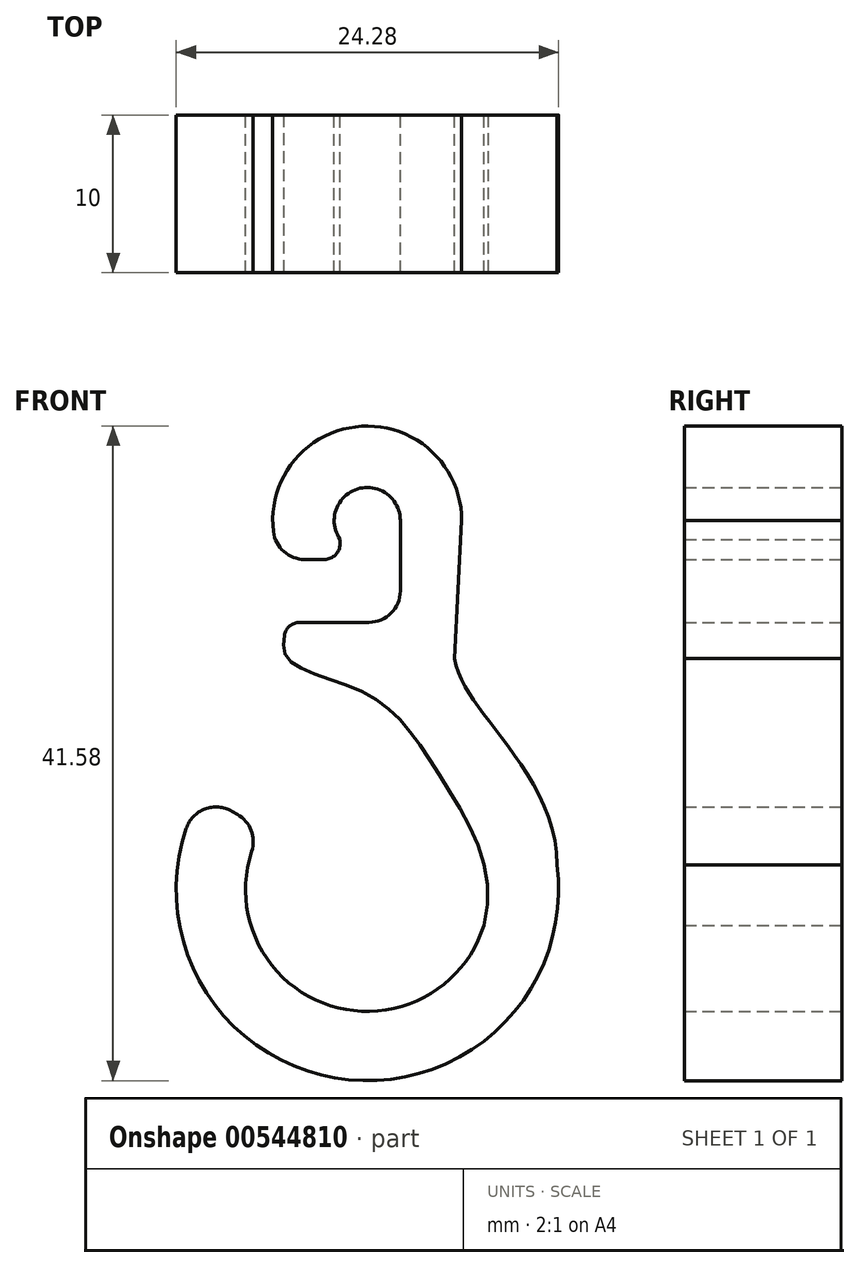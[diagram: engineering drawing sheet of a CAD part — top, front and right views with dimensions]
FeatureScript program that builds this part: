
annotation { "Feature Type Name" : "Feature", "Feature Type Description" : "" }
export const myFeature = defineFeature(function(context is Context, id is Id, definition is map)
    precondition{}
    {
        {
            var Q0;
            Q0=qCreatedBy(makeId("Front.planeOp"),FACE);
            var sketch = newSketch(context, id + "F0", { "sketchPlane" : qUnion([Q0])});
            skCircle(sketch, "E0", {"center": v(0, 0) * mm, "radius": 2.1 * mm});
            skLineSegment(sketch, "E1", {"start": v(2.1, 0) * mm, "end": v(2.1, -8.07) * mm});
            skArc(sketch, "E2", {"start": v(5.47, -2.47) * mm, "mid": v(0, 6) * mm, "end": v(-5.47, -2.47) * mm});
            skLineSegment(sketch, "E3", {"start": v(-5.13, -6.47) * mm, "end": v(-1.73, -6.47) * mm});
            skLineSegment(sketch, "E4", {"start": v(-5.47, -2.47) * mm, "end": v(-1.73, -2.47) * mm});
            skLineSegment(sketch, "E5", {"start": v(-1.73, -2.47) * mm, "end": v(-1.73, -1.2) * mm});
            skLineSegment(sketch, "E6", {"start": v(-1.73, -6.47) * mm, "end": v(-1.73, -6.98) * mm});
            skArc(sketch, "E7", {"start": v(-10.5, -17.36) * mm, "mid": v(-2.37, -35.34) * mm, "end": v(12.05, -21.86) * mm});
            skArc(sketch, "E8.0", {"start": v(-6.7, -19.56) * mm, "mid": v(-3.09, -30.53) * mm, "end": v(7.4, -25.72) * mm});
            skLineSegment(sketch, "E9", {"start": v(-10.5, -17.36) * mm, "end": v(-6.7, -19.56) * mm});
            skLineSegment(sketch, "E10", {"start": v(-1.73, -6.47) * mm, "end": v(2.1, -6.47) * mm});
            skLineSegment(sketch, "E11", {"start": v(6, 0) * mm, "end": v(5.54, -8.76) * mm});
            skFitSpline(sketch, "E12", {"points": [v(5.54, -8.76) * mm, v(7.96, -13.04) * mm, v(12.05, -21.86) * mm], "startDerivative": vector(2.22, -10.9) * mm, "endDerivative": vector(-0.13, -18.18) * mm});
            skFitSpline(sketch, "E13", {"points": [v(-5.13, -6.47) * mm, v(-5.13, -8.67) * mm, v(0, -11.04) * mm, v(4.6, -16.17) * mm, v(7.4, -25.72) * mm], "startDerivative": vector(-1.47, -13.57) * mm, "endDerivative": vector(-9.36, -32.54) * mm});
            skSolve(sketch);
        }
        {
            var Q0;
            Q0=makeQuery(id+"F0.imprint","IMPRINT",FACE,{"disambiguationData":[TD([[makeQuery(id+"F0.imprint","IMPRINT",EDGE,{"derivedFrom":sQuery(id+"F0.wireOp",EDGE,"E7")}),1.0]])]});
            var Q1;
            {var subQ7=sQuery(id+"F0.wireOp",EDGE,"E1");Q1=makeQuery(id+"F0.imprint","IMPRINT",FACE,{"disambiguationData":[TD([[makeQuery(id+"F0.imprint","IMPRINT",EDGE,{"derivedFrom":subQ7}),1.0]])]});}
            var Q2;
            {var subQ0=sQuery(id+"F0.wireOp",EDGE,"oHz4fgxV-5wzr-duW4-scc5-XEAWSv9MsjhE");var subQ1=makeQuery(id+"F0.imprint","INTERSECT",VERTEX,{"derivedFrom":[subQ0,sQuery(id+"F0.wireOp",EDGE,"E1")]});Q2=makeQuery(id+"F0.imprint","IMPRINT",FACE,{"disambiguationData":[TD([[makeQuery(id+"F0.imprint","IMPRINT",EDGE,{"disambiguationData":[TD([[subQ1,-1.0]])],"derivedFrom":subQ0}),1.0]])]});}
            var Q3;
            {var subQ3=sQuery(id+"F0.wireOp",EDGE,"E6");Q3=makeQuery(id+"F0.imprint","IMPRINT",FACE,{"disambiguationData":[TD([[makeQuery(id+"F0.imprint","IMPRINT",EDGE,{"derivedFrom":subQ3}),1.0]])]});}
            extrude(context, id + "F1", {"entities" : qUnion([Q0, Q1, Q2, Q3]), "depth" : 10 * mm, "offsetDistance" : 25 * mm});
        }
        {
            var Q0;
            Q0=makeQuery(id+"F1.opExtrude","SWEPT_EDGE",EDGE,{"disambiguationData":[OSD([sQuery(id+"F0.wireOp",EDGE,"E4"),sQuery(id+"F0.wireOp",EDGE,"E5")])]});
            var Q1;
            Q1=makeQuery(id+"F1.opExtrude","SWEPT_EDGE",EDGE,{"disambiguationData":[OSD([sQuery(id+"F0.wireOp",EDGE,"E3"),sQuery(id+"F0.wireOp",EDGE,"E6")])]});
            fillet(context, id + "F2", {"entities" : qUnion([Q0, Q1]), "radius" : 1 * mm, "tangentPropagation" : true, "allowEdgeOverflow" : false});
        }
        {
            var Q0;
            Q0=makeQuery(id+"F1.opExtrude","SWEPT_EDGE",EDGE,{"disambiguationData":[OSD([sQuery(id+"F0.wireOp",EDGE,"E7"),sQuery(id+"F0.wireOp",EDGE,"E9")])]});
            var Q1;
            Q1=makeQuery(id+"F1.opExtrude","SWEPT_EDGE",EDGE,{"disambiguationData":[OSD([sQuery(id+"F0.wireOp",EDGE,"E8.0"),sQuery(id+"F0.wireOp",EDGE,"E9")])]});
            var Q2;
            Q2=makeQuery(id+"F1.opExtrude","SWEPT_EDGE",EDGE,{"disambiguationData":[OSD([sQuery(id+"F0.wireOp",EDGE,"E2"),sQuery(id+"F0.wireOp",EDGE,"E4")])]});
            var Q3;
            Q3=makeQuery(id+"F1.opExtrude","SWEPT_EDGE",EDGE,{"disambiguationData":[OSD([sQuery(id+"F0.wireOp",EDGE,"BeXxYIan-FhqS-JrBe-bZSa-SEfYxtjjL56G"),sQuery(id+"F0.wireOp",EDGE,"E3")])]});
            fillet(context, id + "F3", {"entities" : qUnion([Q0, Q1, Q2, Q3]), "radius" : 2 * mm, "tangentPropagation" : true, "allowEdgeOverflow" : false});
        }
        {
            var Q0;
            Q0=makeQuery(id+"F1.opExtrude","SWEPT_EDGE",EDGE,{"disambiguationData":[OSD([sQuery(id+"F0.wireOp",EDGE,"E1"),sQuery(id+"F0.wireOp",EDGE,"E10")])]});
            fillet(context, id + "F4", {"entities" : qUnion([Q0]), "radius" : 2 * mm, "tangentPropagation" : true, "allowEdgeOverflow" : false});
        }
    });
